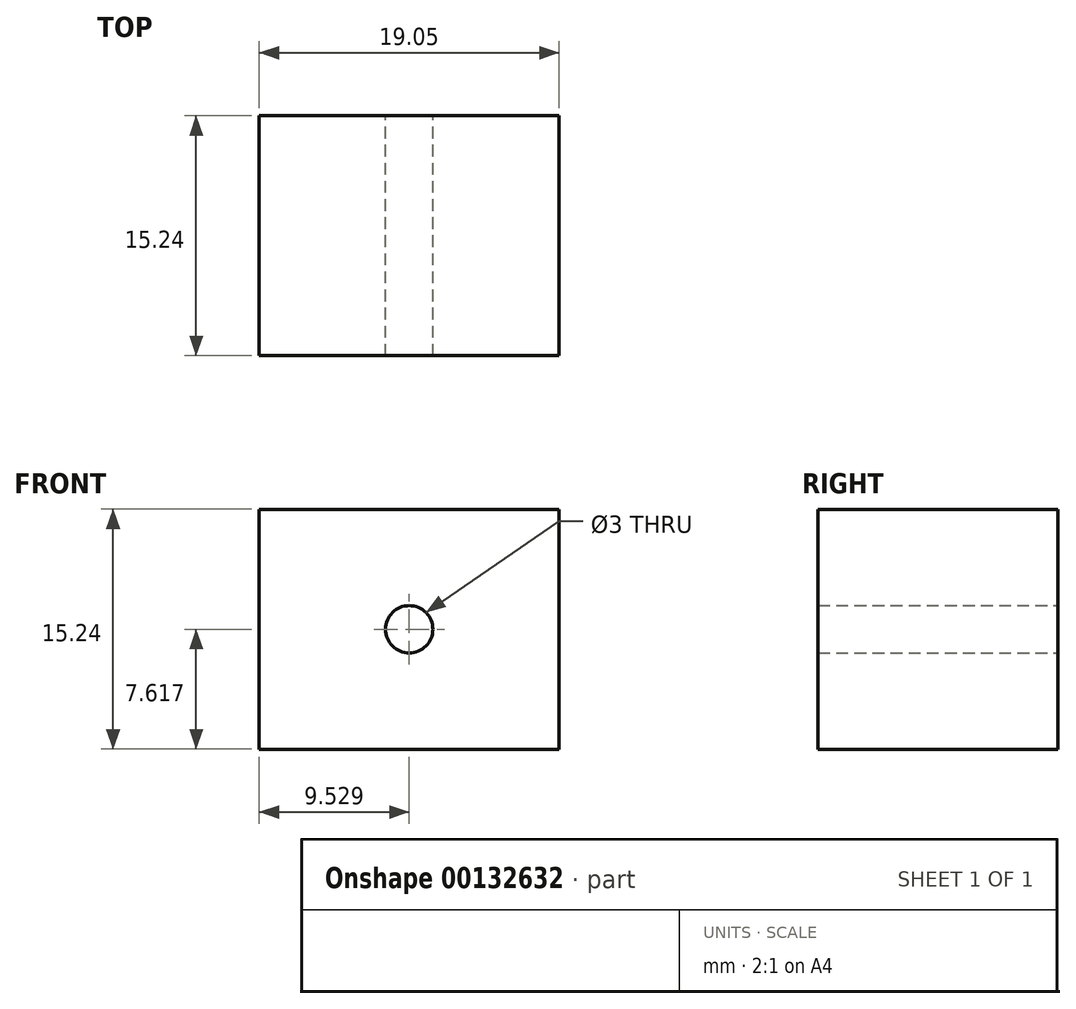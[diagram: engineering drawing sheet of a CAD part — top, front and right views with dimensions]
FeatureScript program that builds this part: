
annotation { "Feature Type Name" : "Feature", "Feature Type Description" : "" }
export const myFeature = defineFeature(function(context is Context, id is Id, definition is map)
    precondition{}
    {
        {
            var Q0;
            Q0=qCreatedBy(makeId("Front.planeOp"),FACE);
            var sketch = newSketch(context, id + "F0", { "sketchPlane" : qUnion([Q0])});
            skLineSegment(sketch, "E0.bottom", {"start": v(-6.78, 6) * mm, "end": v(12.27, 6) * mm});
            skLineSegment(sketch, "E0.top", {"start": v(-6.78, -9.23) * mm, "end": v(12.27, -9.23) * mm});
            skLineSegment(sketch, "E0.left", {"start": v(-6.78, 6) * mm, "end": v(-6.78, -9.23) * mm});
            skLineSegment(sketch, "E0.right", {"start": v(12.27, 6) * mm, "end": v(12.27, -9.23) * mm});
            skCircle(sketch, "E1", {"center": v(2.75, -1.61) * mm, "radius": 1.5 * mm});
            skPoint(sketch, "E1.centerSnap0", {"position": v(2.75, 6) * mm});
            skPoint(sketch, "E1.centerSnap1", {"position": v(12.27, -1.61) * mm});
            skSolve(sketch);
        }
        {
            var Q0;
            Q0 = qSketchRegion(id + "F0", true);
            extrude(context, id + "F1", {"entities" : qUnion([Q0]), "depth" : 15.24 * mm});
        }
    });
